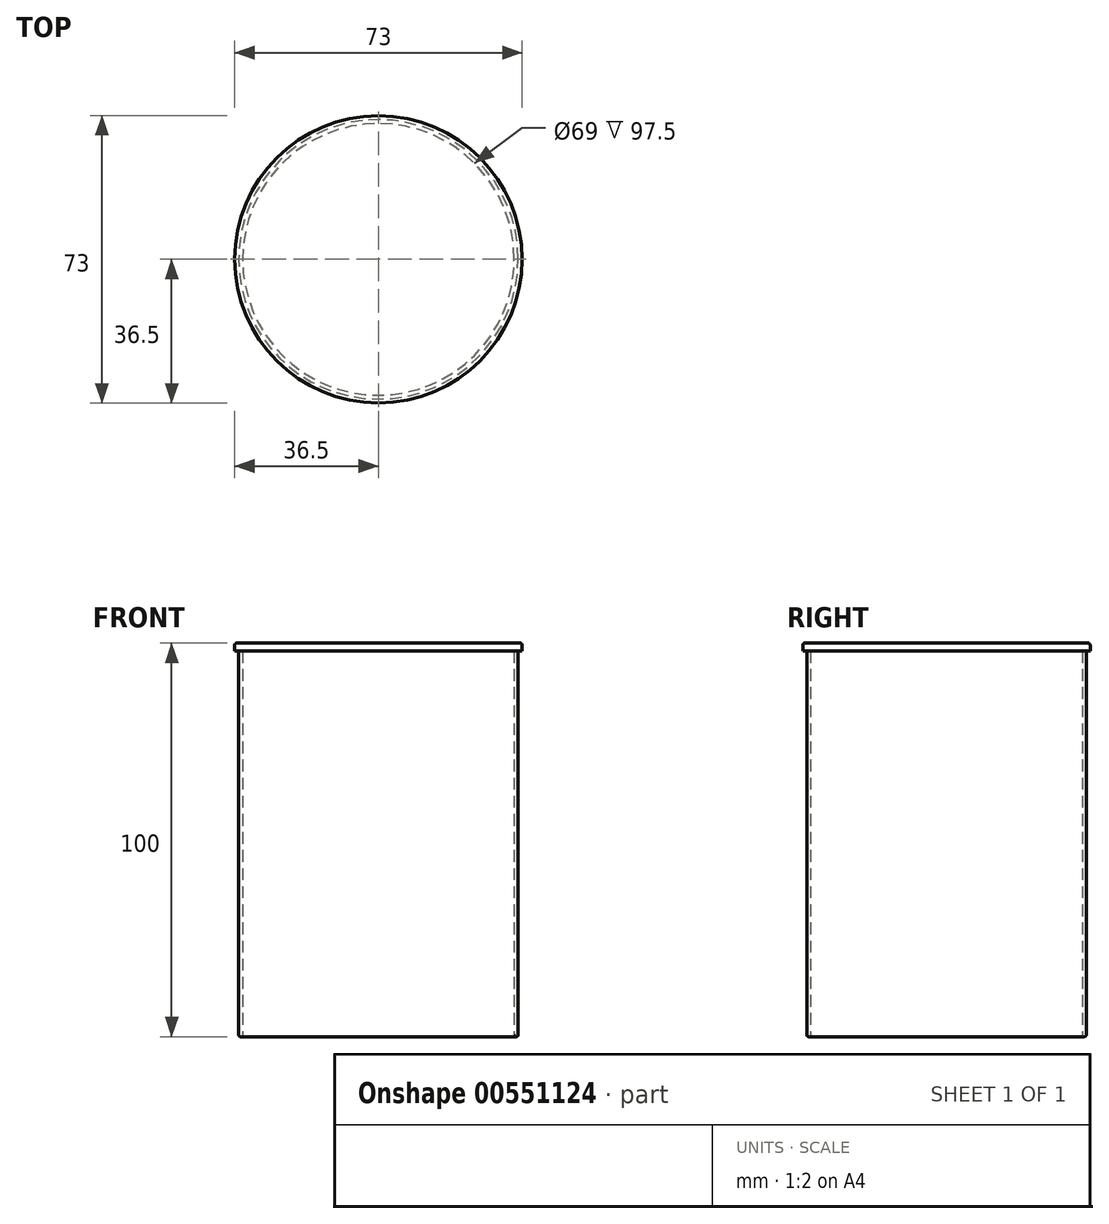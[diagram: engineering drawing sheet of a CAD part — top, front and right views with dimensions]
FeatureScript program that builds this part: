
annotation { "Feature Type Name" : "Feature", "Feature Type Description" : "" }
export const myFeature = defineFeature(function(context is Context, id is Id, definition is map)
    precondition{}
    {
        {
            var Q0;
            Q0=qCreatedBy(makeId("Top.planeOp"),FACE);
            var sketch = newSketch(context, id + "F0", { "sketchPlane" : qUnion([Q0])});
            skCircle(sketch, "E0", {"center": v(0, 0) * mm, "radius": 34.5 * mm});
            skCircle(sketch, "E1.0", {"center": v(0, 0) * mm, "radius": 35.5 * mm});
            skSolve(sketch);
        }
        {
            var Q0;
            Q0=qSketchRegion(id+"F0",true);
            extrude(context, id + "F1", {"entities" : qUnion([Q0]), "depth" : 100 * mm});
        }
        {
            var Q0;
            Q0=makeQuery(id+"F1.opExtrude","CAP_FACE",FACE,{"disambiguationData":[OSD([sQuery(id+"F0.wireOp",EDGE,"E0"),sQuery(id+"F0.wireOp",EDGE,"E1.0")])],"isStart":false});
            var sketch = newSketch(context, id + "F2", { "sketchPlane" : qUnion([Q0])});
            skCircle(sketch, "E2", {"center": v(0, 0) * mm, "radius": 36.5 * mm});
            skSolve(sketch);
        }
        {
            var Q0;
            Q0=qSketchRegion(id+"F2",true);
            extrude(context, id + "F3", {"entities" : qUnion([Q0]), "operationType" : NewBodyOperationType.ADD, "oppositeDirection" : true, "depth" : 2 * mm, "offsetDistance" : 25 * mm});
        }
        {
            var Q0;
            Q0=makeQuery(id+"F1.opExtrude","CAP_FACE",FACE,{"disambiguationData":[OSD([sQuery(id+"F0.wireOp",EDGE,"E0"),sQuery(id+"F0.wireOp",EDGE,"E1.0")])],"isStart":true});
            var Q1;
            Q1=makeQuery(id+"F3.opExtrude","CAP_EDGE",EDGE,{"disambiguationData":[OSD([sQuery(id+"F2.wireOp",EDGE,"E2")])],"isStart":true});
            fillet(context, id + "F4", {"entities" : qUnion([Q0, Q1]), "radius" : .5 * mm, "tangentPropagation" : true, "allowEdgeOverflow" : false});
        }
    });
